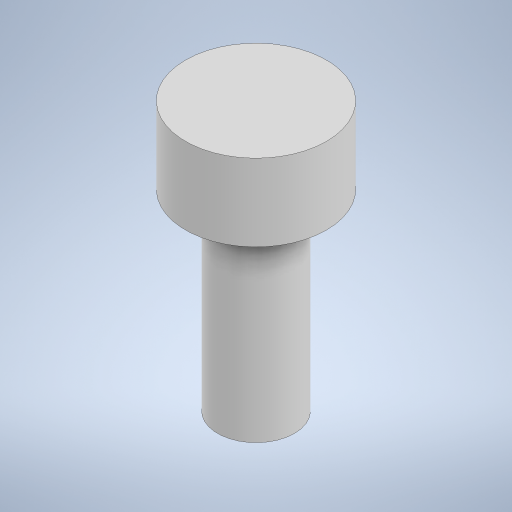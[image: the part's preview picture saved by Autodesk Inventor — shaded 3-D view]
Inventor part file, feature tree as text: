
AUTODESK INVENTOR PART (.ipt)
format: ipt  version: 2024 (Build 280153000, 153)  size: 239,616 bytes
history: native  units: mm
features: extrude x2, sketch x2
ambient origin geometry x8: Origin, YZ Plane, XZ Plane, XY Plane, X Axis, Y Axis, Z Axis, Center Point
bodies: Solid1 (feature_tree)
feature tree (4):
  extrude  "Extrusion1"  Depth=3.0mm TaperAngle=0.0deg
  extrude  "Extrusion2"  Depth=7.5mm TaperAngle=0.0deg
  sketch  "Sketch1"  dims[d0=5.5mm d1=3.0mm d2=0.0mm]
  sketch  "Sketch2"  dims[d3=3.0mm d4=7.5mm d5=0.0mm]
